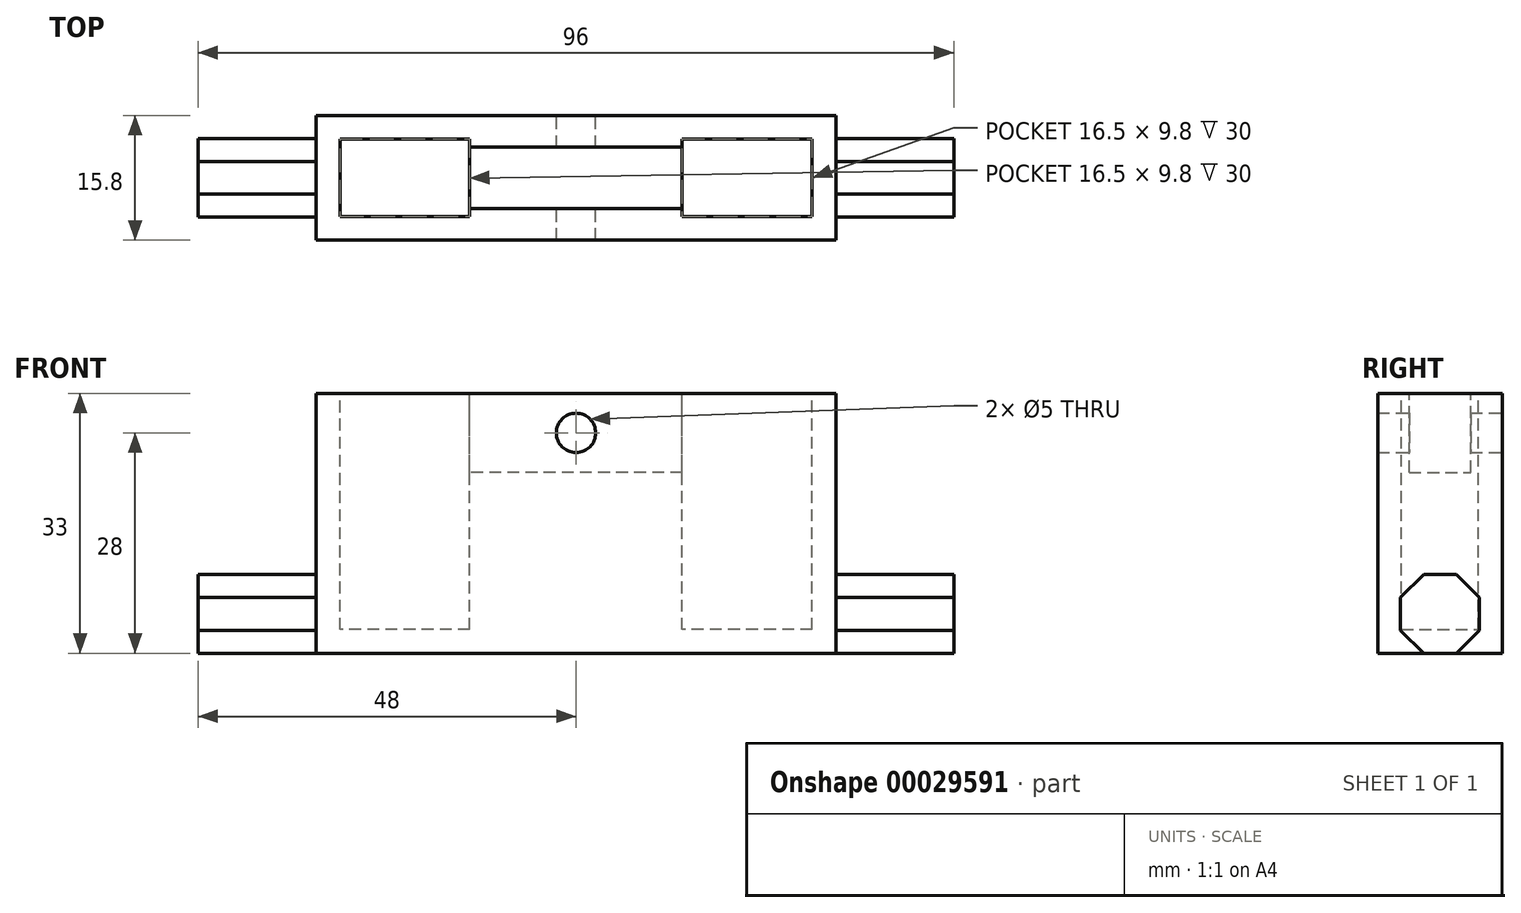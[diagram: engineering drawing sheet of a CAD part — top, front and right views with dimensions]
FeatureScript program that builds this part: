
annotation { "Feature Type Name" : "Feature", "Feature Type Description" : "" }
export const myFeature = defineFeature(function(context is Context, id is Id, definition is map)
    precondition{}
    {
        {
            var Q0;
            Q0=qCreatedBy(makeId("Top.planeOp"),FACE);
            var sketch = newSketch(context, id + "F0", { "sketchPlane" : qUnion([Q0])});
            skLineSegment(sketch, "E0.rect.bottom", {"start": v(30, -4.9) * mm, "end": v(-30, -4.9) * mm});
            skLineSegment(sketch, "E0.rect.top", {"start": v(30, 4.9) * mm, "end": v(-30, 4.9) * mm});
            skLineSegment(sketch, "E0.rect.left", {"start": v(30, -4.9) * mm, "end": v(30, 4.9) * mm});
            skLineSegment(sketch, "E0.rect.right", {"start": v(-30, -4.9) * mm, "end": v(-30, 4.9) * mm});
            skPoint(sketch, "E0.rect.middle", {"position": v(0, 0) * mm});
            skLineSegment(sketch, "E1.0", {"start": v(-33, -7.9) * mm, "end": v(-33, 7.9) * mm});
            skLineSegment(sketch, "E1.1", {"start": v(33, -7.9) * mm, "end": v(-33, -7.9) * mm});
            skLineSegment(sketch, "E1.2", {"start": v(33, -7.9) * mm, "end": v(33, 7.9) * mm});
            skLineSegment(sketch, "E1.3", {"start": v(33, 7.9) * mm, "end": v(-33, 7.9) * mm});
            skLineSegment(sketch, "E2", {"start": v(-33, 0) * mm, "end": v(33, 0) * mm, "construction": true});
            skLineSegment(sketch, "E3", {"start": v(0, 4.9) * mm, "end": v(0, -4.9) * mm, "construction": true});
            skLineSegment(sketch, "E4.rect.bottom", {"start": v(13.5, 3.9) * mm, "end": v(-13.5, 3.9) * mm});
            skLineSegment(sketch, "E4.rect.top", {"start": v(13.5, 4.9) * mm, "end": v(-13.5, 4.9) * mm});
            skLineSegment(sketch, "E4.rect.left", {"start": v(13.5, 3.9) * mm, "end": v(13.5, 4.9) * mm});
            skLineSegment(sketch, "E4.rect.right", {"start": v(-13.5, 3.9) * mm, "end": v(-13.5, 4.9) * mm});
            skPoint(sketch, "E4.rect.middle", {"position": v(0, 4.4) * mm});
            skLineSegment(sketch, "E5.MirrorCS", {"start": v(13.5, -3.9) * mm, "end": v(13.5, -4.9) * mm});
            skLineSegment(sketch, "E6.MirrorCS", {"start": v(-13.5, -3.9) * mm, "end": v(-13.5, -4.9) * mm});
            skPoint(sketch, "E7.MirrorP", {"position": v(0, -4.4) * mm});
            skLineSegment(sketch, "E8.MirrorCS", {"start": v(13.5, -3.9) * mm, "end": v(-13.5, -3.9) * mm});
            skLineSegment(sketch, "E9.MirrorCS", {"start": v(13.5, -4.9) * mm, "end": v(-13.5, -4.9) * mm});
            skSolve(sketch);
        }
        {
            var Q0;
            {var subQ3=sQuery(id+"F0.wireOp",EDGE,"E0.rect.left");Q0=makeQuery(id+"F0.imprint","IMPRINT",FACE,{"disambiguationData":[TD([[makeQuery(id+"F0.imprint","IMPRINT",EDGE,{"derivedFrom":subQ3}),-1.0]])]});}
            var Q1;
            Q1=makeQuery(id+"F0.imprint","IMPRINT",FACE,{"disambiguationData":[TD([[makeQuery(id+"F0.imprint","IMPRINT",EDGE,{"derivedFrom":sQuery(id+"F0.wireOp",EDGE,"E5.MirrorCS")}),-1.0]])]});
            var Q2;
            Q2=makeQuery(id+"F0.imprint","IMPRINT",FACE,{"disambiguationData":[TD([[makeQuery(id+"F0.imprint","IMPRINT",EDGE,{"derivedFrom":sQuery(id+"F0.wireOp",EDGE,"E4.rect.bottom")}),-1.0]])]});
            var Q3;
            {var subQ4=sQuery(id+"F0.wireOp",EDGE,"E0.rect.left");Q3=makeQuery(id+"F0.imprint","IMPRINT",FACE,{"disambiguationData":[TD([[makeQuery(id+"F0.imprint","IMPRINT",EDGE,{"derivedFrom":subQ4}),1.0]])]});}
            extrude(context, id + "F1", {"entities" : qUnion([Q0, Q1, Q2, Q3]), "depth" : 33 * mm});
        }
        {
            var Q0;
            {var subQ4=sQuery(id+"F0.wireOp",EDGE,"E0.rect.left");Q0=makeQuery(id+"F0.imprint","IMPRINT",FACE,{"disambiguationData":[TD([[makeQuery(id+"F0.imprint","IMPRINT",EDGE,{"derivedFrom":subQ4}),1.0]])]});}
            extrude(context, id + "F2", {"entities" : qUnion([Q0]), "operationType" : NewBodyOperationType.REMOVE, "depth" : 10 * mm});
        }
        {
            var Q0;
            Q0=makeQuery(id+"F2.boolean.opBoolean","COPY",FACE,{"derivedFrom":makeQuery(id+"F2.opExtrude","SWEPT_FACE",FACE,{"disambiguationData":[OSD([sQuery(id+"F0.wireOp",EDGE,"E8.MirrorCS")])]})});
            var sketch = newSketch(context, id + "F3", { "sketchPlane" : qUnion([Q0])});
            skLineSegment(sketch, "E10", {"start": v(0, 10) * mm, "end": v(0, 5) * mm, "construction": true});
            skLineSegment(sketch, "E11", {"start": v(0, 5) * mm, "end": v(0, 2.5) * mm, "construction": true});
            skLineSegment(sketch, "E12", {"start": v(0, 2.5) * mm, "end": v(0, 0) * mm, "construction": true});
            skCircle(sketch, "E13", {"center": v(0, 5) * mm, "radius": 2.5 * mm});
            skSolve(sketch);
        }
        {
            var Q0;
            Q0=makeQuery(id+"F3.imprint","IMPRINT",FACE,{"disambiguationData":[TD([[makeQuery(id+"F3.imprint","IMPRINT",EDGE,{"derivedFrom":sQuery(id+"F3.wireOp",EDGE,"E13")}),1.0]])]});
            extrude(context, id + "F4", {"entities" : qUnion([Q0]), "operationType" : NewBodyOperationType.REMOVE, "endBound" : BoundingType.THROUGH_ALL, "depth" : 25 * mm, "hasSecondDirection" : true, "secondDirectionBound" : SecondDirectionBoundingType.THROUGH_ALL, "secondDirectionOppositeDirection" : true, "secondDirectionDepth" : 25 * mm});
        }
        {
            var Q0;
            Q0=makeQuery(id+"F1.opExtrude","SWEPT_FACE",FACE,{"disambiguationData":[OSD([sQuery(id+"F0.wireOp",EDGE,"E1.2")])]});
            var sketch = newSketch(context, id + "F5", { "sketchPlane" : qUnion([Q0])});
            skLineSegment(sketch, "E14", {"start": v(0, 0) * mm, "end": v(0, 33) * mm, "construction": true});
            skLineSegment(sketch, "E15.bottom", {"start": v(0, 33) * mm, "end": v(-5, 33) * mm, "construction": true});
            skLineSegment(sketch, "E15.top", {"start": v(0, 28) * mm, "end": v(-5, 28) * mm, "construction": true});
            skLineSegment(sketch, "E15.left", {"start": v(0, 33) * mm, "end": v(0, 28) * mm, "construction": true});
            skLineSegment(sketch, "E15.right", {"start": v(-5, 33) * mm, "end": v(-5, 28) * mm, "construction": true});
            skLineSegment(sketch, "E16", {"start": v(-5, 28) * mm, "end": v(-5, 30.07) * mm});
            skLineSegment(sketch, "E17", {"start": v(-5, 30.07) * mm, "end": v(-3.54, 31.54) * mm});
            skLineSegment(sketch, "E18", {"start": v(-2.07, 33) * mm, "end": v(0, 33) * mm});
            skLineSegment(sketch, "E19", {"start": v(-3.54, 31.54) * mm, "end": v(-2.07, 33) * mm});
            skLineSegment(sketch, "E20.MirrorCS", {"start": v(5, 28) * mm, "end": v(5, 30.07) * mm});
            skLineSegment(sketch, "E21.MirrorCS", {"start": v(5, 30.07) * mm, "end": v(3.54, 31.54) * mm});
            skLineSegment(sketch, "E22.MirrorCS", {"start": v(3.54, 31.54) * mm, "end": v(2.07, 33) * mm});
            skLineSegment(sketch, "E23.MirrorCS", {"start": v(2.07, 33) * mm, "end": v(0, 33) * mm});
            skLineSegment(sketch, "E24.MirrorCS", {"start": v(-5, 28) * mm, "end": v(-5, 25.93) * mm});
            skLineSegment(sketch, "E25.MirrorCS", {"start": v(-5, 25.93) * mm, "end": v(-3.54, 24.46) * mm});
            skLineSegment(sketch, "E26.MirrorCS", {"start": v(-3.54, 24.46) * mm, "end": v(-2.07, 23) * mm});
            skLineSegment(sketch, "E27.MirrorCS", {"start": v(-2.07, 23) * mm, "end": v(0, 23) * mm});
            skLineSegment(sketch, "E28.MirrorCS", {"start": v(2.07, 23) * mm, "end": v(0, 23) * mm});
            skLineSegment(sketch, "E29.MirrorCS", {"start": v(3.54, 24.46) * mm, "end": v(2.07, 23) * mm});
            skLineSegment(sketch, "E30.MirrorCS", {"start": v(5, 25.93) * mm, "end": v(3.54, 24.46) * mm});
            skLineSegment(sketch, "E31.MirrorCS", {"start": v(5, 28) * mm, "end": v(5, 25.93) * mm});
            skSolve(sketch);
        }
        {
            var Q0;
            Q0=makeQuery(id+"F5.imprint","IMPRINT",FACE,{"disambiguationData":[TD([[makeQuery(id+"F5.imprint","IMPRINT",EDGE,{"derivedFrom":sQuery(id+"F5.wireOp",EDGE,"E16")}),-1.0]])]});
            extrude(context, id + "F6", {"entities" : qUnion([Q0]), "operationType" : NewBodyOperationType.ADD, "depth" : 15 * mm});
        }
        {
            var Q0;
            Q0=makeQuery(id+"F1.opExtrude","SWEPT_FACE",FACE,{"disambiguationData":[OSD([sQuery(id+"F0.wireOp",EDGE,"E1.0")])]});
            var sketch = newSketch(context, id + "F7", { "sketchPlane" : qUnion([Q0])});
            skLineSegment(sketch, "E32.0.0", {"start": v(5, 30.07) * mm, "end": v(5, 25.93) * mm});
            skLineSegment(sketch, "E32.0.1", {"start": v(5, 25.93) * mm, "end": v(2.07, 23) * mm});
            skLineSegment(sketch, "E32.0.2", {"start": v(2.07, 23) * mm, "end": v(-2.07, 23) * mm});
            skLineSegment(sketch, "E32.0.3", {"start": v(-2.07, 23) * mm, "end": v(-5, 25.93) * mm});
            skLineSegment(sketch, "E32.0.4", {"start": v(-5, 25.93) * mm, "end": v(-5, 30.07) * mm});
            skLineSegment(sketch, "E32.0.5", {"start": v(-5, 30.07) * mm, "end": v(-2.07, 33) * mm});
            skLineSegment(sketch, "E32.0.6", {"start": v(-2.07, 33) * mm, "end": v(2.07, 33) * mm});
            skLineSegment(sketch, "E32.0.7", {"start": v(2.07, 33) * mm, "end": v(5, 30.07) * mm});
            skSolve(sketch);
        }
        {
            var Q0;
            Q0=makeQuery(id+"F6.opExtrude","CAP_FACE",FACE,{"disambiguationData":[OSD([sQuery(id+"F5.wireOp",EDGE,"E16"),sQuery(id+"F5.wireOp",EDGE,"E17"),sQuery(id+"F5.wireOp",EDGE,"E18"),sQuery(id+"F5.wireOp",EDGE,"E19"),sQuery(id+"F5.wireOp",EDGE,"E20.MirrorCS"),sQuery(id+"F5.wireOp",EDGE,"E21.MirrorCS"),sQuery(id+"F5.wireOp",EDGE,"E22.MirrorCS"),sQuery(id+"F5.wireOp",EDGE,"E23.MirrorCS"),sQuery(id+"F5.wireOp",EDGE,"E24.MirrorCS"),sQuery(id+"F5.wireOp",EDGE,"E25.MirrorCS"),sQuery(id+"F5.wireOp",EDGE,"E26.MirrorCS"),sQuery(id+"F5.wireOp",EDGE,"E27.MirrorCS"),sQuery(id+"F5.wireOp",EDGE,"E28.MirrorCS"),sQuery(id+"F5.wireOp",EDGE,"E29.MirrorCS"),sQuery(id+"F5.wireOp",EDGE,"E30.MirrorCS"),sQuery(id+"F5.wireOp",EDGE,"E31.MirrorCS")])],"isStart":false});
            var Q1;
            Q1=makeQuery(id+"F7.imprint","IMPRINT",FACE,{"disambiguationData":[TD([[makeQuery(id+"F7.imprint","IMPRINT",EDGE,{"derivedFrom":sQuery(id+"F7.wireOp",EDGE,"E32.0.0")}),-1.0]])]});
            extrude(context, id + "F8", {"entities" : qUnion([Q0, Q1]), "operationType" : NewBodyOperationType.ADD, "oppositeDirection" : true, "depth" : 15 * mm});
        }
        {
            var Q0;
            Q0=makeQuery(id+"F1.opExtrude","SWEPT_BODY",BODY,{"disambiguationData":[OSD([sQuery(id+"F0.wireOp",EDGE,"E1.0"),sQuery(id+"F0.wireOp",EDGE,"E1.1"),sQuery(id+"F0.wireOp",EDGE,"E1.2"),sQuery(id+"F0.wireOp",EDGE,"E1.3")])]});
            var Q1;
            Q1=qCreatedBy(makeId("Top.planeOp"),FACE);
            mirror(context, id + "F9", {"entities" : qUnion([Q0]), "mirrorPlane" : qUnion([Q1])});
        }
        {
            var Q0;
            Q0=makeQuery(id+"F9.opPattern","COPY",BODY,{"derivedFrom":makeQuery(id+"F1.opExtrude","SWEPT_BODY",BODY,{"disambiguationData":[OSD([sQuery(id+"F0.wireOp",EDGE,"E1.0"),sQuery(id+"F0.wireOp",EDGE,"E1.1"),sQuery(id+"F0.wireOp",EDGE,"E1.2"),sQuery(id+"F0.wireOp",EDGE,"E1.3")])]}),"instanceName":"1"});
            deleteBodies(context, id + "F10", {"entities" : qUnion([Q0])});
        }
        {
            var Q0;
            Q0=makeQuery(id+"F1.opExtrude","SWEPT_BODY",BODY,{"disambiguationData":[OSD([sQuery(id+"F0.wireOp",EDGE,"E1.0"),sQuery(id+"F0.wireOp",EDGE,"E1.1"),sQuery(id+"F0.wireOp",EDGE,"E1.2"),sQuery(id+"F0.wireOp",EDGE,"E1.3")])]});
            var Q1;
            Q1=sQuery(id+"F0.wireOp",EDGE,"E2");
            transform(context, id + "F11", {"entities" : qUnion([Q0]), "transformType" : TransformType.ROTATION, "transformAxis" : qUnion([Q1]), "angle" : 180 * degree, "makeCopy" : false});
        }
        {
            var Q0;
            Q0=makeQuery(id+"F2.boolean.opBoolean","COPY",FACE,{"derivedFrom":makeQuery(id+"F2.opExtrude","CAP_FACE",FACE,{"disambiguationData":[OSD([sQuery(id+"F0.wireOp",EDGE,"E0.rect.bottom"),sQuery(id+"F0.wireOp",EDGE,"E0.rect.top"),sQuery(id+"F0.wireOp",EDGE,"E0.rect.left"),sQuery(id+"F0.wireOp",EDGE,"E0.rect.right"),sQuery(id+"F0.wireOp",EDGE,"E4.rect.bottom"),sQuery(id+"F0.wireOp",EDGE,"E4.rect.left"),sQuery(id+"F0.wireOp",EDGE,"E4.rect.right"),sQuery(id+"F0.wireOp",EDGE,"E5.MirrorCS"),sQuery(id+"F0.wireOp",EDGE,"E6.MirrorCS"),sQuery(id+"F0.wireOp",EDGE,"E8.MirrorCS")])],"isStart":false})});
            var sketch = newSketch(context, id + "F12", { "sketchPlane" : qUnion([Q0])});
            skLineSegment(sketch, "E33", {"start": v(13.5, -3.9) * mm, "end": v(13.5, 3.9) * mm});
            skLineSegment(sketch, "E34", {"start": v(-13.5, 3.9) * mm, "end": v(-13.5, -3.9) * mm});
            skSolve(sketch);
        }
        {
            var Q0;
            Q0=makeQuery(id+"F12.imprint","IMPRINT",FACE,{"disambiguationData":[TD([[makeQuery(id+"F12.imprint","IMPRINT",EDGE,{"derivedFrom":sQuery(id+"F12.wireOp",EDGE,"E34")}),-1.0]])]});
            var Q1;
            Q1=makeQuery(id+"F12.imprint","IMPRINT",FACE,{"disambiguationData":[TD([[makeQuery(id+"F12.imprint","IMPRINT",EDGE,{"derivedFrom":sQuery(id+"F12.wireOp",EDGE,"E33")}),-1.0]])]});
            extrude(context, id + "F13", {"entities" : qUnion([Q0, Q1]), "operationType" : NewBodyOperationType.REMOVE, "oppositeDirection" : true, "depth" : 20 * mm});
        }
    });
